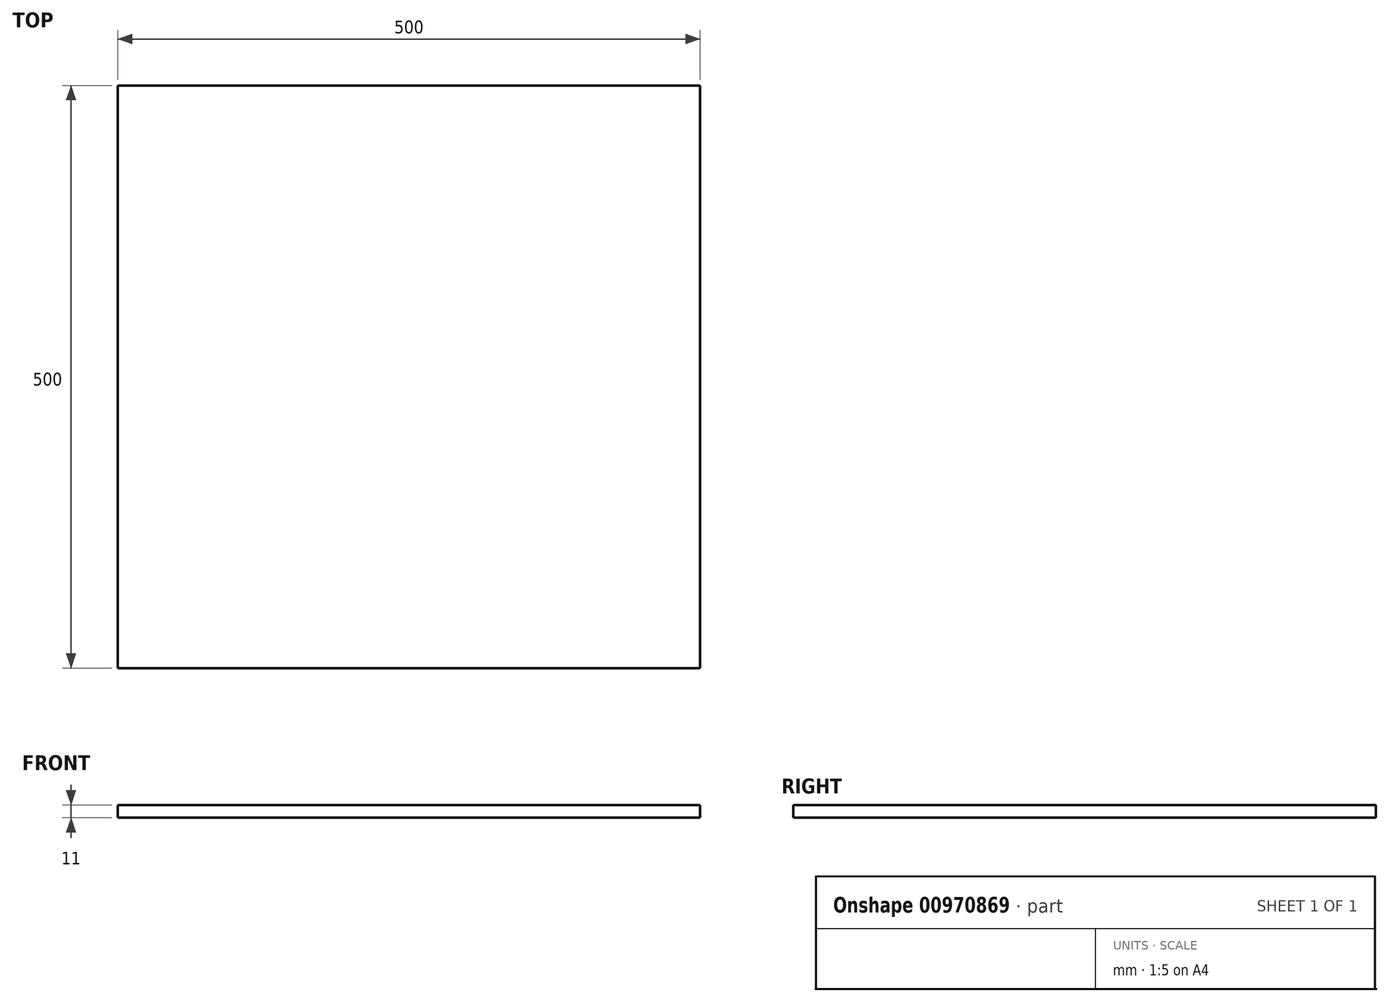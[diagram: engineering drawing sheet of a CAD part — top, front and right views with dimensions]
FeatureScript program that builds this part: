
annotation { "Feature Type Name" : "Feature", "Feature Type Description" : "" }
export const myFeature = defineFeature(function(context is Context, id is Id, definition is map)
    precondition{}
    {
        {
            var Q0;
            Q0=qCreatedBy(makeId("Top.planeOp"),FACE);
            var sketch = newSketch(context, id + "F0", { "sketchPlane" : qUnion([Q0])});
            skLineSegment(sketch, "E0.bottom", {"start": v(-453.6, 469.57) * mm, "end": v(46.4, 469.57) * mm});
            skLineSegment(sketch, "E0.top", {"start": v(-453.6, -30.43) * mm, "end": v(46.4, -30.43) * mm});
            skLineSegment(sketch, "E0.left", {"start": v(-453.6, 469.57) * mm, "end": v(-453.6, -30.43) * mm});
            skLineSegment(sketch, "E0.right", {"start": v(46.4, 469.57) * mm, "end": v(46.4, -30.43) * mm});
            skSolve(sketch);
        }
        {
            var Q0;
            Q0 = qSketchRegion(id + "F0", true);
            extrude(context, id + "F1", {"entities" : qUnion([Q0]), "depth" : 11 * mm, "offsetDistance" : 25 * mm});
        }
    });
